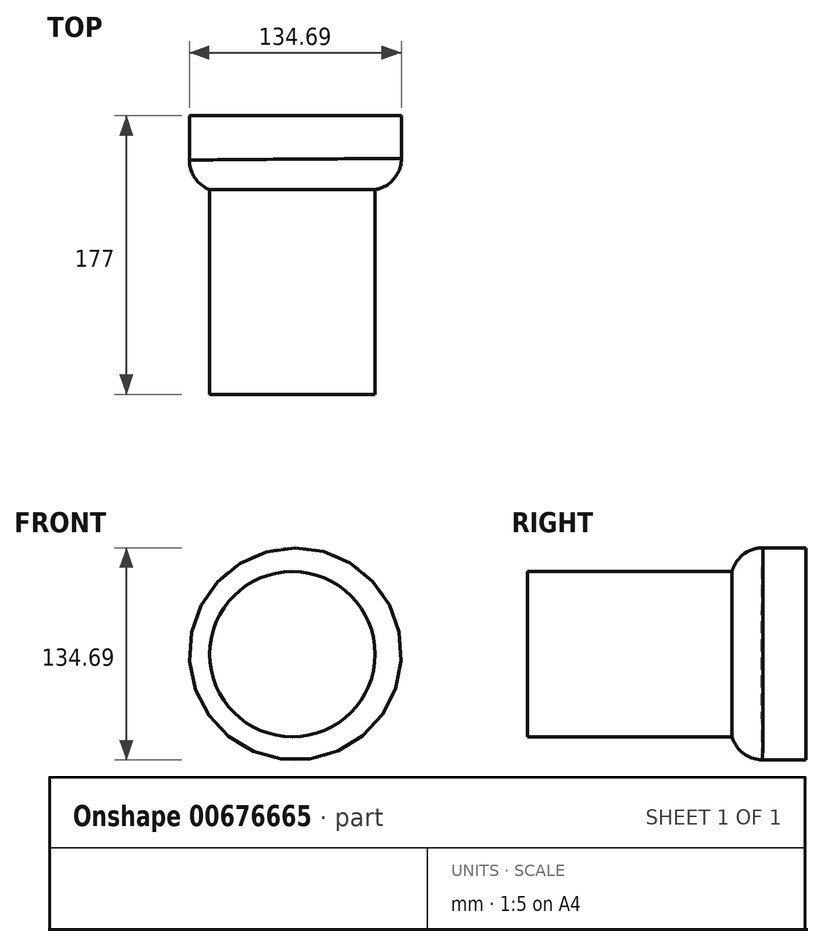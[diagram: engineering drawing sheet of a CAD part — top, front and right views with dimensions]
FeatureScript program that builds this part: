
annotation { "Feature Type Name" : "Feature", "Feature Type Description" : "" }
export const myFeature = defineFeature(function(context is Context, id is Id, definition is map)
    precondition{}
    {
        {
            var Q0;
            Q0=qCreatedBy(makeId("Front.planeOp"),FACE);
            var sketch = newSketch(context, id + "F0", { "sketchPlane" : qUnion([Q0])});
            skCircle(sketch, "E0", {"center": v(27.28, 27.36) * mm, "radius": 52.47 * mm});
            skSolve(sketch);
        }
        {
            var Q0;
            Q0 = qSketchRegion(id + "F0", true);
            extrude(context, id + "F1", {"entities" : qUnion([Q0]), "depth" : 130 * mm, "offsetDistance" : 25 * mm});
        }
        {
            var Q0;
            Q0=makeQuery(id+"F1.opExtrude","CAP_FACE",FACE,{"disambiguationData":[OSD([sQuery(id+"F0.wireOp",EDGE,"E0")])],"isStart":true});
            var sketch = newSketch(context, id + "F2", { "sketchPlane" : qUnion([Q0])});
            skCircle(sketch, "E1", {"center": v(-27.28, 27.36) * mm, "radius": 51.65 * mm});
            skSolve(sketch);
        }
        {
            var Q0;
            Q0=makeQuery(id+"F2.imprint","IMPRINT",FACE,{"disambiguationData":[TD([[makeQuery(id+"F2.imprint","IMPRINT",EDGE,{"derivedFrom":sQuery(id+"F2.wireOp",EDGE,"E1")}),1.0]])]});
            var sketch = newSketch(context, id + "F3", { "sketchPlane" : qUnion([Q0])});
            skCircle(sketch, "E2", {"center": v(-29.2, 27.58) * mm, "radius": 67.35 * mm});
            skSolve(sketch);
        }
        {
            var Q0;
            Q0 = qSketchRegion(id + "F3", true);
            extrude(context, id + "F4", {"entities" : qUnion([Q0]), "operationType" : NewBodyOperationType.ADD, "depth" : 47 * mm, "offsetDistance" : 25 * mm});
        }
        {
            var Q0;
            Q0=makeQuery(id+"F4.opExtrude","CAP_EDGE",EDGE,{"disambiguationData":[OSD([sQuery(id+"F3.wireOp",EDGE,"E2")])],"isStart":true});
            fillet(context, id + "F5", {"entities" : qUnion([Q0]), "radius" : 20 * mm, "tangentPropagation" : true, "allowEdgeOverflow" : false});
        }
        {
            var Q0;
            Q0=makeQuery(id+"F4.opExtrude","CAP_FACE",FACE,{"disambiguationData":[OSD([sQuery(id+"F3.wireOp",EDGE,"E2")])],"isStart":false});
            var sketch = newSketch(context, id + "F6", { "sketchPlane" : qUnion([Q0])});
            skLineSegment(sketch, "E3", {"start": v(-42.34, -38.47) * mm, "end": v(-561.96, -394.31) * mm});
            skLineSegment(sketch, "E4", {"start": v(-95.73, 17.2) * mm, "end": v(-618.44, -340.38) * mm});
            skArc(sketch, "E5", {"start": v(-618.44, -340.38) * mm, "mid": v(-633.94, -413.16) * mm, "end": v(-561.96, -394.31) * mm});
            skArc(sketch, "E6", {"start": v(-42.34, -38.47) * mm, "mid": v(-36.21, 20.85) * mm, "end": v(-95.73, 17.2) * mm});
            skSolve(sketch);
        }
        {
            var Q0;
            {var subQ0=sQuery(id+"F6.wireOp",EDGE,"E3");Q0=makeQuery(id+"F6.imprint","IMPRINT",FACE,{"disambiguationData":[TD([[makeQuery(id+"F6.imprint","IMPRINT",EDGE,{"derivedFrom":subQ0}),-1.0]])]});}
            extrude(context, id + "F7", {"entities" : qUnion([Q0]), "operationType" : NewBodyOperationType.REMOVE, "depth" : 16 * mm, "offsetDistance" : 25 * mm});
        }
    });
